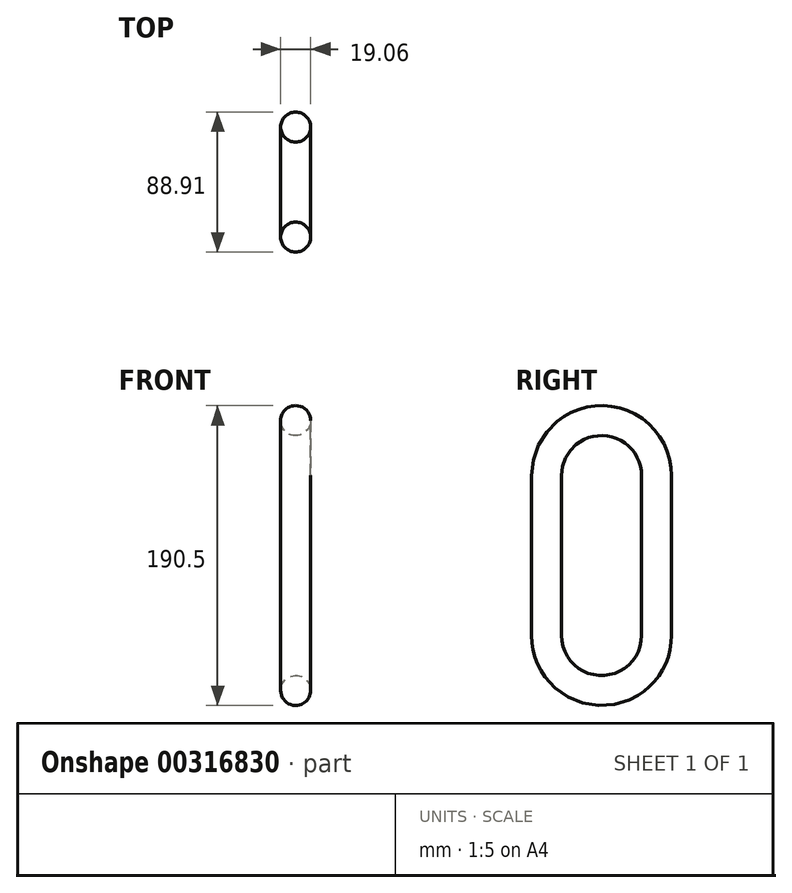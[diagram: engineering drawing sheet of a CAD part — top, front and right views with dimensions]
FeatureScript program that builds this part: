
annotation { "Feature Type Name" : "Feature", "Feature Type Description" : "" }
export const myFeature = defineFeature(function(context is Context, id is Id, definition is map)
    precondition{}
    {
        {
            var Q0;
            Q0=qCreatedBy(makeId("Right.planeOp"),FACE);
            var sketch = newSketch(context, id + "F0", { "sketchPlane" : qUnion([Q0])});
            skLineSegment(sketch, "E0", {"start": v(0, 0) * mm, "end": v(0, 101.6) * mm});
            skLineSegment(sketch, "E1", {"start": v(69.85, 0) * mm, "end": v(69.85, 101.6) * mm});
            skArc(sketch, "E2", {"start": v(69.85, 101.6) * mm, "mid": v(34.93, 136.53) * mm, "end": v(0, 101.6) * mm});
            skArc(sketch, "E3", {"start": v(0, 0) * mm, "mid": v(34.93, -34.93) * mm, "end": v(69.85, 0) * mm});
            skLineSegment(sketch, "E4", {"start": v(0, 53.1) * mm, "end": v(69.85, 53.1) * mm, "construction": true});
            skLineSegment(sketch, "E5", {"start": v(34.93, 53.1) * mm, "end": v(34.93, 136.53) * mm, "construction": true});
            skSolve(sketch);
        }
        {
            var Q0;
            Q0=qCreatedBy(makeId("Top.planeOp"),FACE);
            var sketch = newSketch(context, id + "F1", { "sketchPlane" : qUnion([Q0])});
            skCircle(sketch, "E6", {"center": v(0, 0) * mm, "radius": 9.53 * mm});
            skSolve(sketch);
        }
        {
            var Q0;
            Q0=makeQuery(id+"F1.imprint","IMPRINT",FACE,{"disambiguationData":[TD([[makeQuery(id+"F1.imprint","IMPRINT",EDGE,{"derivedFrom":sQuery(id+"F1.wireOp",EDGE,"E6")}),1.0]])]});
            var Q1;
            Q1=sQuery(id+"F0.wireOp",EDGE,"E3");
            var Q2;
            Q2=sQuery(id+"F0.wireOp",EDGE,"E1");
            var Q3;
            Q3=sQuery(id+"F0.wireOp",EDGE,"E2");
            var Q4;
            Q4=sQuery(id+"F0.wireOp",EDGE,"E0");
            sweep(context, id + "F2", {"profiles" : qUnion([Q0]), "path" : qUnion([Q1, Q2, Q3, Q4])});
        }
    });
